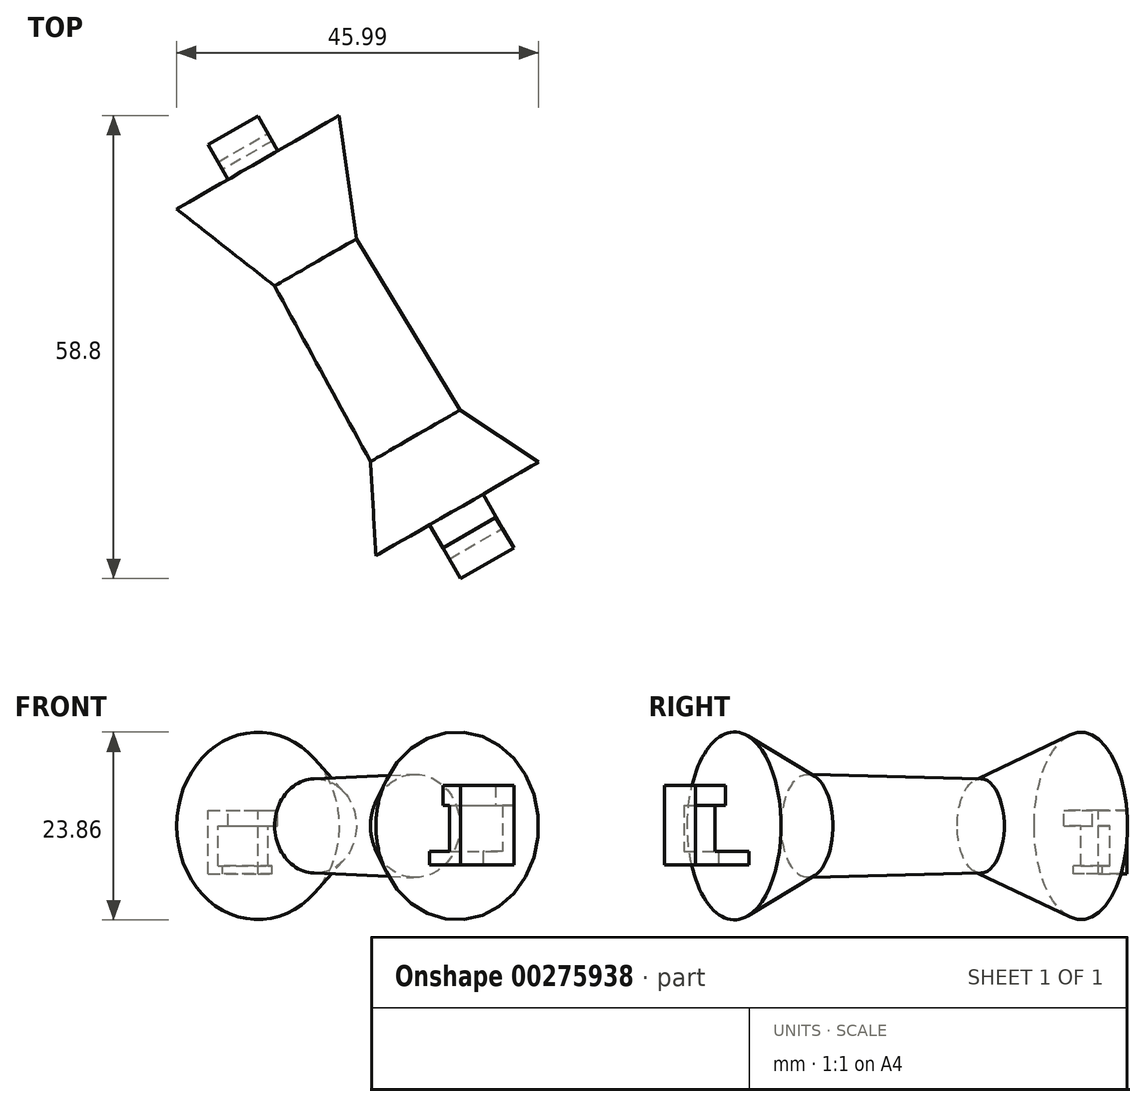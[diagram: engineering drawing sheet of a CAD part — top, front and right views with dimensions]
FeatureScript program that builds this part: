
annotation { "Feature Type Name" : "Feature", "Feature Type Description" : "" }
export const myFeature = defineFeature(function(context is Context, id is Id, definition is map)
    precondition{}
    {
        {
            var Q0;
            Q0=qCreatedBy(makeId("Top.planeOp"),FACE);
            var sketch = newSketch(context, id + "F0", { "sketchPlane" : qUnion([Q0])});
            skLineSegment(sketch, "E0", {"start": v(-3.42, 6.37) * mm, "end": v(9.74, -15.37) * mm});
            skLineSegment(sketch, "E1", {"start": v(9.74, -15.37) * mm, "end": v(19.74, -21.97) * mm});
            skLineSegment(sketch, "E2", {"start": v(-15.94, 16.11) * mm, "end": v(9.4, -27.92) * mm, "construction": true});
            skLineSegment(sketch, "E3", {"start": v(-15.94, 16.11) * mm, "end": v(9.4, -27.92) * mm});
            skPoint(sketch, "E4.end.orphan", {"position": v(-15.94, 0) * mm});
            skPoint(sketch, "E5.orphan", {"position": v(-3.42, -33.24) * mm});
            skLineSegment(sketch, "E6", {"start": v(9.4, -27.92) * mm, "end": v(19.74, -21.97) * mm});
            skPoint(sketch, "E7.end.orphan", {"position": v(-3.42, 22.04) * mm});
            skLineSegment(sketch, "E8", {"start": v(-15.94, 16.11) * mm, "end": v(-5.63, 22.04) * mm});
            skLineSegment(sketch, "E9", {"start": v(-5.63, 22.04) * mm, "end": v(-3.42, 6.37) * mm});
            skSolve(sketch);
        }
        {
            var Q0;
            Q0=makeQuery(id+"F0.imprint","IMPRINT",FACE,{"disambiguationData":[TD([[makeQuery(id+"F0.imprint","IMPRINT",EDGE,{"derivedFrom":sQuery(id+"F0.wireOp",EDGE,"E0")}),-1.0]])]});
            var Q1;
            Q1=sQuery(id+"F0.wireOp",EDGE,"E3");
            revolve(context, id + "F1", {"entities" : qUnion([Q0]), "axis" : qUnion([Q1]), "revolveType" : RevolveType.FULL});
        }
        {
            var Q0;
            Q0=makeQuery(id+"F1.opRevolve","SWEPT_FACE",FACE,{"disambiguationData":[OSD([sQuery(id+"F0.wireOp",EDGE,"E6")])]});
            var sketch = newSketch(context, id + "F2", { "sketchPlane" : qUnion([Q0])});
            skLineSegment(sketch, "E10.bottom", {"start": v(-9.83, -3.25) * mm, "end": v(-2, -3.25) * mm});
            skLineSegment(sketch, "E10.top", {"start": v(-9.83, -4.94) * mm, "end": v(-2, -4.94) * mm});
            skLineSegment(sketch, "E10.left", {"start": v(-9.83, -3.25) * mm, "end": v(-9.83, -4.94) * mm});
            skLineSegment(sketch, "E10.right", {"start": v(-2, -3.25) * mm, "end": v(-2, -4.94) * mm});
            skSolve(sketch);
        }
        {
            var Q0;
            Q0=makeQuery(id+"F2.imprint","IMPRINT",FACE,{"disambiguationData":[TD([[makeQuery(id+"F2.imprint","IMPRINT",EDGE,{"derivedFrom":sQuery(id+"F2.wireOp",EDGE,"E10.bottom")}),-1.0]])]});
            extrude(context, id + "F3", {"entities" : qUnion([Q0]), "operationType" : NewBodyOperationType.ADD, "depth" : 7.87 * mm});
        }
        {
            var Q0;
            Q0=makeQuery(id+"F3.opExtrude","SWEPT_FACE",FACE,{"disambiguationData":[OSD([sQuery(id+"F2.wireOp",EDGE,"E10.bottom")])]});
            var sketch = newSketch(context, id + "F4", { "sketchPlane" : qUnion([Q0])});
            skLineSegment(sketch, "E11", {"start": v(8.39, -34.28) * mm, "end": v(15.17, -30.38) * mm});
            skLineSegment(sketch, "E12", {"start": v(15.17, -30.38) * mm, "end": v(16.6, -32.86) * mm});
            skLineSegment(sketch, "E13", {"start": v(16.6, -32.86) * mm, "end": v(9.81, -36.76) * mm});
            skLineSegment(sketch, "E14", {"start": v(9.81, -36.76) * mm, "end": v(8.39, -34.28) * mm});
            skSolve(sketch);
        }
        {
            var Q0;
            Q0=makeQuery(id+"F4.imprint","IMPRINT",FACE,{"disambiguationData":[TD([[makeQuery(id+"F4.imprint","IMPRINT",EDGE,{"derivedFrom":sQuery(id+"F4.wireOp",EDGE,"E11")}),-1.0]])]});
            extrude(context, id + "F5", {"entities" : qUnion([Q0]), "operationType" : NewBodyOperationType.ADD, "depth" : 5.84 * mm});
        }
        {
            var Q0;
            Q0=makeQuery(id+"F5.opExtrude","CAP_FACE",FACE,{"disambiguationData":[OSD([sQuery(id+"F4.wireOp",EDGE,"E11"),sQuery(id+"F4.wireOp",EDGE,"E12"),sQuery(id+"F4.wireOp",EDGE,"E13"),sQuery(id+"F4.wireOp",EDGE,"E14")])],"isStart":false});
            var sketch = newSketch(context, id + "F6", { "sketchPlane" : qUnion([Q0])});
            skLineSegment(sketch, "E15", {"start": v(16.6, -32.86) * mm, "end": v(9.81, -36.76) * mm});
            skLineSegment(sketch, "E16", {"start": v(9.81, -36.76) * mm, "end": v(7.57, -32.86) * mm});
            skLineSegment(sketch, "E17", {"start": v(7.57, -32.86) * mm, "end": v(14.25, -29.02) * mm});
            skLineSegment(sketch, "E18", {"start": v(14.25, -29.02) * mm, "end": v(16.6, -32.86) * mm});
            skSolve(sketch);
        }
        {
            var Q0;
            Q0 = qSketchRegion(id + "F6", true);
            extrude(context, id + "F7", {"entities" : qUnion([Q0]), "operationType" : NewBodyOperationType.ADD, "depth" : 2.54 * mm});
        }
        {
            var Q0;
            Q0=makeQuery(id+"F1.opRevolve","SWEPT_FACE",FACE,{"disambiguationData":[OSD([sQuery(id+"F0.wireOp",EDGE,"E8")])]});
            var sketch = newSketch(context, id + "F8", { "sketchPlane" : qUnion([Q0])});
            skLineSegment(sketch, "E19.bottom", {"start": v(10.14, 0) * mm, "end": v(2.85, 0) * mm});
            skLineSegment(sketch, "E19.top", {"start": v(10.14, 1.95) * mm, "end": v(2.85, 1.95) * mm});
            skLineSegment(sketch, "E19.left", {"start": v(10.14, 0) * mm, "end": v(10.14, 1.95) * mm});
            skLineSegment(sketch, "E19.right", {"start": v(2.85, 0) * mm, "end": v(2.85, 1.95) * mm});
            skSolve(sketch);
        }
        {
            var Q0;
            Q0 = qSketchRegion(id + "F8", true);
            extrude(context, id + "F9", {"entities" : qUnion([Q0]), "operationType" : NewBodyOperationType.ADD, "depth" : 5.08 * mm});
        }
        {
            var Q0;
            Q0=makeQuery(id+"F9.opExtrude","SWEPT_FACE",FACE,{"disambiguationData":[OSD([sQuery(id+"F8.wireOp",EDGE,"E19.bottom")])]});
            var sketch = newSketch(context, id + "F10", { "sketchPlane" : qUnion([Q0])});
            skLineSegment(sketch, "E20", {"start": v(-15.93, -21.98) * mm, "end": v(-22.25, -18.34) * mm});
            skLineSegment(sketch, "E21", {"start": v(-22.25, -18.34) * mm, "end": v(-20.99, -16.14) * mm});
            skLineSegment(sketch, "E22", {"start": v(-20.99, -16.14) * mm, "end": v(-14.67, -19.78) * mm});
            skLineSegment(sketch, "E23", {"start": v(-14.67, -19.78) * mm, "end": v(-15.93, -21.98) * mm});
            skSolve(sketch);
        }
        {
            var Q0;
            Q0 = qSketchRegion(id + "F10", true);
            extrude(context, id + "F11", {"entities" : qUnion([Q0]), "operationType" : NewBodyOperationType.ADD, "depth" : 5.08 * mm});
        }
        {
            var Q0;
            Q0=makeQuery(id+"F11.opExtrude","CAP_FACE",FACE,{"disambiguationData":[OSD([sQuery(id+"F10.wireOp",EDGE,"E20"),sQuery(id+"F10.wireOp",EDGE,"E21"),sQuery(id+"F10.wireOp",EDGE,"E22"),sQuery(id+"F10.wireOp",EDGE,"E23")])],"isStart":false});
            var sketch = newSketch(context, id + "F12", { "sketchPlane" : qUnion([Q0])});
            skLineSegment(sketch, "E24", {"start": v(-15.93, -21.98) * mm, "end": v(-14.12, -18.83) * mm});
            skLineSegment(sketch, "E25", {"start": v(-14.12, -18.83) * mm, "end": v(-20.44, -15.2) * mm});
            skLineSegment(sketch, "E26", {"start": v(-22.25, -18.34) * mm, "end": v(-15.93, -21.98) * mm});
            skLineSegment(sketch, "E27", {"start": v(-22.25, -18.34) * mm, "end": v(-20.44, -15.2) * mm});
            skPoint(sketch, "E28.orphan", {"position": v(-20.99, -14.88) * mm});
            skSolve(sketch);
        }
        {
            var Q0;
            Q0 = qSketchRegion(id + "F12", true);
            extrude(context, id + "F13", {"entities" : qUnion([Q0]), "operationType" : NewBodyOperationType.ADD, "depth" : 1.02 * mm});
        }
    });
